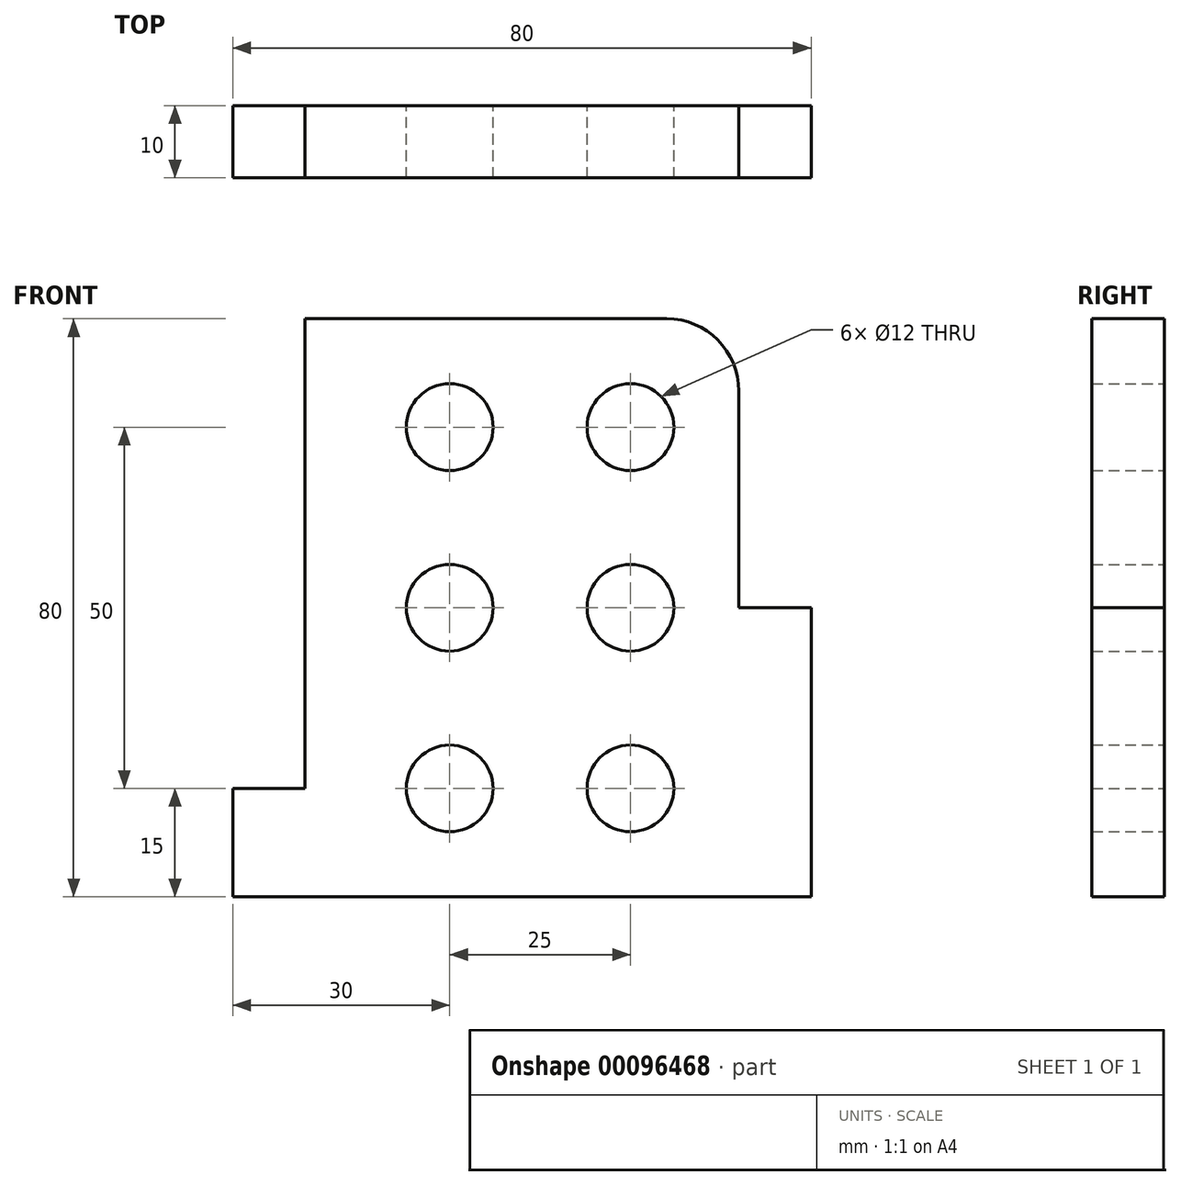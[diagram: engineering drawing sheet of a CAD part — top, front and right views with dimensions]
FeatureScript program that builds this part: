
annotation { "Feature Type Name" : "Feature", "Feature Type Description" : "" }
export const myFeature = defineFeature(function(context is Context, id is Id, definition is map)
    precondition{}
    {
        {
            var Q0;
            Q0=qCreatedBy(makeId("Front.planeOp"),FACE);
            var sketch = newSketch(context, id + "F0", { "sketchPlane" : qUnion([Q0])});
            skLineSegment(sketch, "E0", {"start": v(0, 0) * mm, "end": v(80, 0) * mm});
            skLineSegment(sketch, "E1", {"start": v(80, 0) * mm, "end": v(80, 40) * mm});
            skLineSegment(sketch, "E2", {"start": v(80, 40) * mm, "end": v(70, 40) * mm});
            skLineSegment(sketch, "E3", {"start": v(70, 40) * mm, "end": v(70, 70) * mm});
            skLineSegment(sketch, "E4", {"start": v(60, 80) * mm, "end": v(10, 80) * mm});
            skLineSegment(sketch, "E5", {"start": v(10, 80) * mm, "end": v(10, 15) * mm});
            skLineSegment(sketch, "E6", {"start": v(10, 15) * mm, "end": v(0, 15) * mm});
            skLineSegment(sketch, "E7", {"start": v(0, 15) * mm, "end": v(0, 0) * mm});
            skCircle(sketch, "E8", {"center": v(30, 15) * mm, "radius": 6 * mm});
            skCircle(sketch, "E9", {"center": v(55, 15) * mm, "radius": 6 * mm});
            skCircle(sketch, "E10", {"center": v(30, 40) * mm, "radius": 6 * mm});
            skCircle(sketch, "E11", {"center": v(55, 40) * mm, "radius": 6 * mm});
            skCircle(sketch, "E12", {"center": v(30, 65) * mm, "radius": 6 * mm});
            skCircle(sketch, "E13", {"center": v(55, 65) * mm, "radius": 6 * mm});
            skLineSegment(sketch, "E14", {"start": v(10, 65) * mm, "end": v(70, 65) * mm, "construction": true});
            skLineSegment(sketch, "E15", {"start": v(30, 80) * mm, "end": v(30, 0) * mm, "construction": true});
            skLineSegment(sketch, "E16", {"start": v(55, 80) * mm, "end": v(55, 0) * mm, "construction": true});
            skLineSegment(sketch, "E17", {"start": v(10, 40) * mm, "end": v(70, 40) * mm, "construction": true});
            skLineSegment(sketch, "E18", {"start": v(10, 15) * mm, "end": v(80, 15) * mm, "construction": true});
            skPoint(sketch, "E19.visualSharp", {"position": v(70, 80) * mm});
            skArc(sketch, "E19.filletArc", {"start": v(70, 70) * mm, "mid": v(67.07, 77.07) * mm, "end": v(60, 80) * mm});
            skSolve(sketch);
        }
        {
            var Q0;
            Q0 = qSketchRegion(id + "F0", true);
            extrude(context, id + "F1", {"entities" : qUnion([Q0]), "depth" : 10 * mm});
        }
    });
